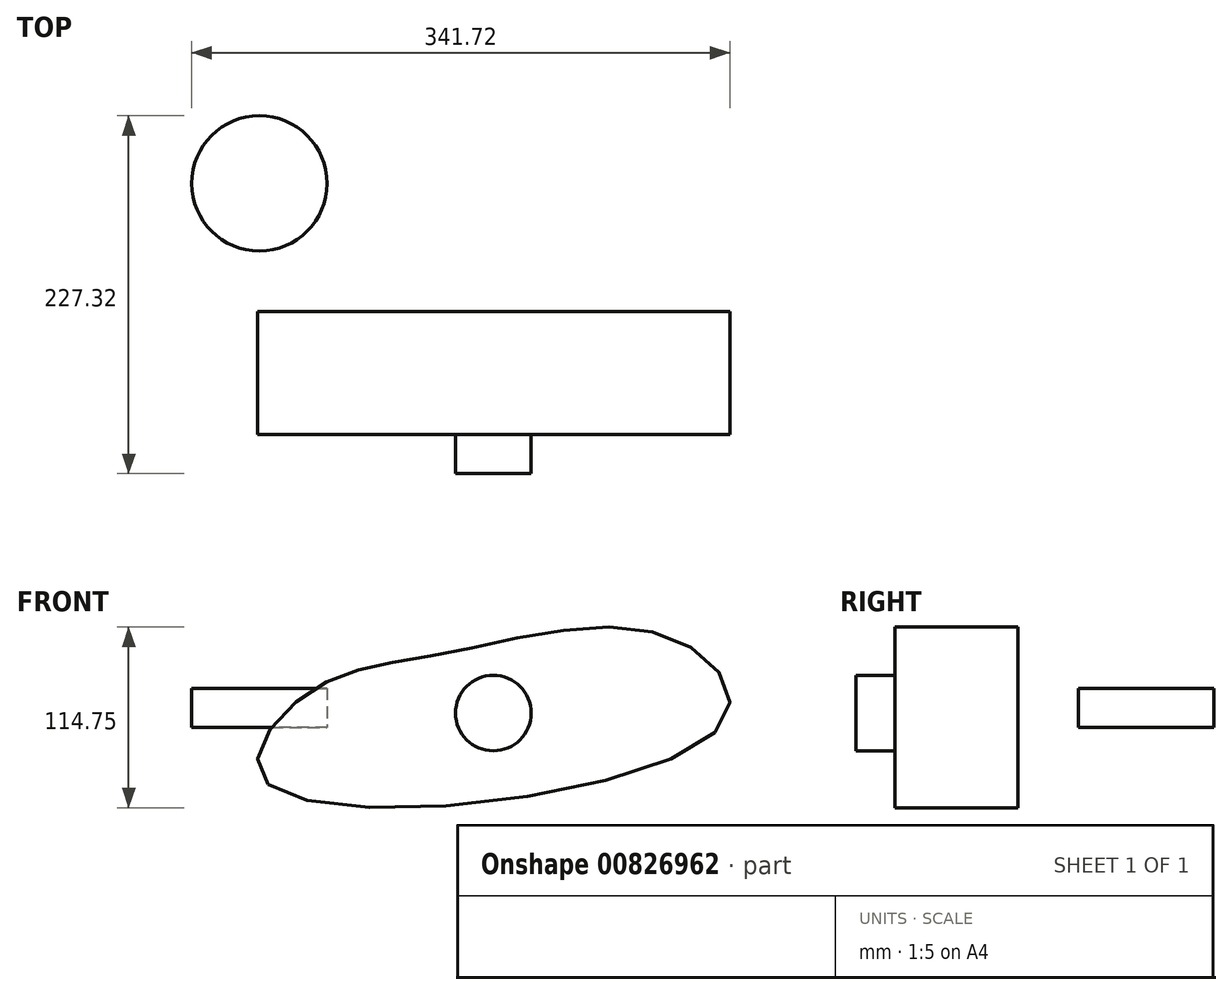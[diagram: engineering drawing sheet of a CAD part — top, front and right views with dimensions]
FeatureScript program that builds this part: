
annotation { "Feature Type Name" : "Feature", "Feature Type Description" : "" }
export const myFeature = defineFeature(function(context is Context, id is Id, definition is map)
    precondition{}
    {
        {
            var Q0;
            Q0=qCreatedBy(makeId("Front.planeOp"),FACE);
            var sketch = newSketch(context, id + "F0", { "sketchPlane" : qUnion([Q0])});
            skFitSpline(sketch, "E0", {"points": [v(-143.14, -36) * mm, v(-119.32, 21.04) * mm, v(-30.15, 47.29) * mm, v(111.22, 57.7) * mm, v(143.64, 0) * mm, v(-143.14, -36) * mm]});
            skSolve(sketch);
        }
        {
            var Q0;
            Q0=makeQuery(id+"F0.imprint","IMPRINT",FACE,{"disambiguationData":[TD([[makeQuery(id+"F0.imprint","IMPRINT",EDGE,{"derivedFrom":sQuery(id+"F0.wireOp",EDGE,"E0")}),-1.0]])]});
            extrude(context, id + "F1", {"entities" : qUnion([Q0]), "depth" : 78 * mm, "offsetDistance" : 25 * mm});
        }
        {
            var Q0;
            Q0=makeQuery(id+"F1.opExtrude","CAP_FACE",FACE,{"disambiguationData":[OSD([sQuery(id+"F0.wireOp",EDGE,"E0")])],"isStart":false});
            var sketch = newSketch(context, id + "F2", { "sketchPlane" : qUnion([Q0])});
            skCircle(sketch, "E1", {"center": v(0, 9.25) * mm, "radius": 24 * mm});
            skSolve(sketch);
        }
        {
            var Q0;
            Q0=makeQuery(id+"F2.imprint","IMPRINT",FACE,{"disambiguationData":[TD([[makeQuery(id+"F2.imprint","IMPRINT",EDGE,{"derivedFrom":sQuery(id+"F2.wireOp",EDGE,"E1")}),1.0]])]});
            extrude(context, id + "F3", {"entities" : qUnion([Q0]), "operationType" : NewBodyOperationType.ADD, "depth" : 25 * mm, "offsetDistance" : 25 * mm});
        }
        {
            var Q0;
            Q0=qCreatedBy(makeId("Top.planeOp"),FACE);
            var sketch = newSketch(context, id + "F4", { "sketchPlane" : qUnion([Q0])});
            skCircle(sketch, "E2", {"center": v(-148.56, 81.34) * mm, "radius": 42.99 * mm});
            skSolve(sketch);
        }
        {
            var Q0;
            Q0=makeQuery(id+"F4.imprint","IMPRINT",FACE,{"disambiguationData":[TD([[makeQuery(id+"F4.imprint","IMPRINT",EDGE,{"derivedFrom":sQuery(id+"F4.wireOp",EDGE,"E2")}),1.0]])]});
            extrude(context, id + "F5", {"entities" : qUnion([Q0]), "depth" : 25 * mm, "offsetDistance" : 25 * mm});
        }
    });
